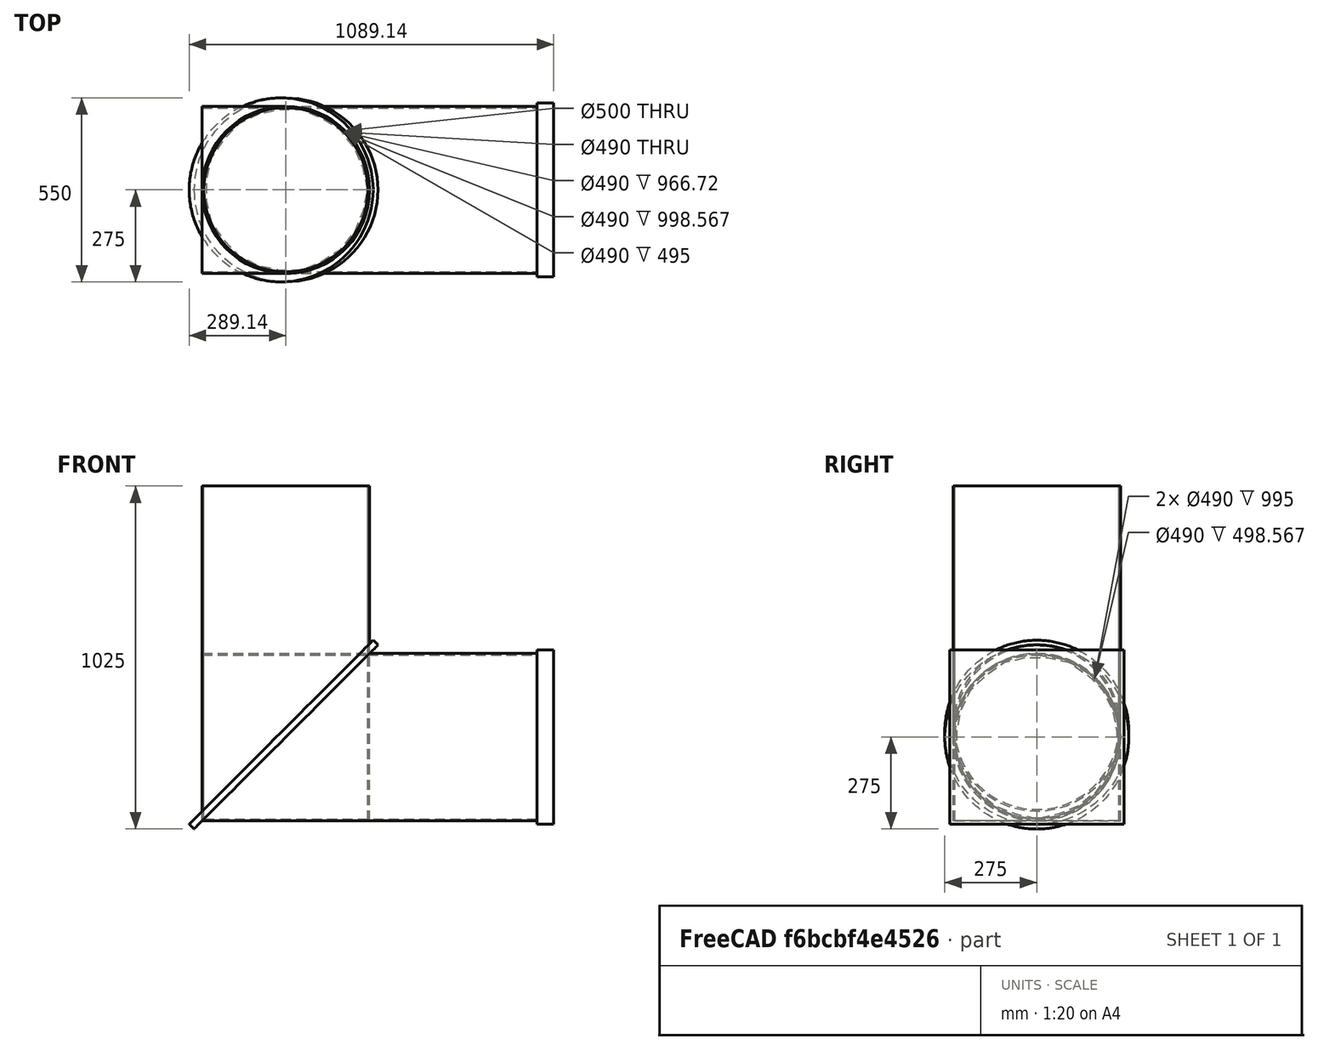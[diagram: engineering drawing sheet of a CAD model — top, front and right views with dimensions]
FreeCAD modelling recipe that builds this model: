
FCSTD DOCUMENT  (FreeCAD 0.21R33694 (Git))
Label: Tube_Corner
License: All rights reserved
LicenseURL: http://en.wikipedia.org/wiki/All_rights_reserved
objects: Part::FeaturePython×7, Part::Feature×3, Part::Plane×2, Part::Extrusion×2, Fem::ConstraintForce×2, Sketcher::SketchObject×1, Part::Face×1, App::MaterialObjectPython×1, Fem::FemSolverObjectPython×1, Fem::ConstraintFixed×1, Fem::FemMeshObjectPython×1, Fem::FemAnalysis×1
note: 16 computed .brp shape members not serialized (recipe doc carries the construction recipe); baked Part::Feature solids carry a one-line shape summary decoded from their .brp

FEATURE [Part::FeaturePython] Tube  # WARN: FeaturePython — macro-defined, semantics opaque (R4)
  AttacherType = Attacher::AttachEngine3D
  Height = 1000
  InnerRadius = 245
  OuterRadius = 250
FEATURE [Part::FeaturePython] Tube001  # WARN: FeaturePython — macro-defined, semantics opaque (R4)
  AttacherType = Attacher::AttachEngine3D
  Height = 1000
  InnerRadius = 245
  OuterRadius = 250
  Placement = pos=(-250,0,250) rot=(0,1,0;1.5708rad)
FEATURE [Part::Plane] Plane
  AttacherType = Attacher::AttachEngine3D
  Length = 1000
  Placement = pos=(-250,-250,0) rot=(0,-1,0;0.785398rad)
  Width = 500
FEATURE [Part::Plane] Plane001
  AttacherType = Attacher::AttachEngine3D
  Length = 1000
  Placement = pos=(-250,-250,0) rot=(0,-1,0;0.785398rad)
  Width = 500
FEATURE [Part::FeaturePython] Slice  # WARN: FeaturePython — macro-defined, semantics opaque (R4)
  Base = -> Tube
  Mode = 1
  Tolerance = 0
  Tools = -> [Plane]
FEATURE [Part::FeaturePython] Slice001  # WARN: FeaturePython — macro-defined, semantics opaque (R4)
  Base = -> Tube001
  Mode = 1
  Tolerance = 0
  Tools = -> [Plane001]
FEATURE [Sketcher::SketchObject] Sketch
  FullyConstrained = true
  MapMode = 5
  Placement = pos=(750,0,1.67e-13) rot=(0.57735,0.57735,0.57735;2.0944rad)
  sketch-geometry (4):
    g0: LineSegment StartX=-260 StartY=510 StartZ=0 EndX=260 EndY=510 EndZ=0
    g1: LineSegment StartX=260 StartY=510 StartZ=0 EndX=260 EndY=-10 EndZ=0
    g2: LineSegment StartX=260 StartY=-10 StartZ=0 EndX=-260 EndY=-10 EndZ=0
    g3: LineSegment StartX=-260 StartY=-10 StartZ=0 EndX=-260 EndY=510 EndZ=0
  constraints (12):
    c: Coincident(g0,g1)
    c: Coincident(g1,g2)
    c: Coincident(g2,g3)
    c: Coincident(g3,g0)
    c: Horizontal(g0)
    c: Horizontal(g2)
    c: Vertical(g1)
    c: Vertical(g3)
    c: DistanceY(g1,g-1) = 10
    c: DistanceX(g2,g-1) = 260
    c: DistanceX(g-1,g1) = 260
    c: DistanceY(g1,g1) = 520
FEATURE [Part::Face] Face
  FaceMakerClass = Part::FaceMakerBullseye
  Sources = -> [Sketch]
FEATURE [Part::Extrusion] Extrude
  Base = -> Face
  Dir = (1,0,0)
  DirMode = 2
  FaceMakerClass = Part::FaceMakerBullseye
  LengthFwd = 50
  LengthRev = 0
  Solid = false
  Symmetric = false
FEATURE [App::MaterialObjectPython] MaterialSolid  # material (typed FeaturePython)
  Category = 0
  Material = AuthorAndLicense=(c) 2014 M. Münch - GNU Lesser General Public License (LGPL),CardName=Steel-St-E-315,Density=7800 kg/m^3,Father=Metal,+13 more (map truncated)
FEATURE [Fem::FemSolverObjectPython] SolverCcxTools  # FEM object (typed FeaturePython)
  AnalysisType = 0
  BeamShellResultOutput3D = false
  BucklingFactors = 1
  EigenmodeHighLimit = 1000000
  EigenmodeLowLimit = 0
  EigenmodesCount = 10
  GeometricalNonlinearity = 0
  IterationsControlParameterCutb = 0.25,0.5,0.75,0.85,,,1.5,
  IterationsControlParameterIter = 4,8,9,200,10,400,,200,,
  IterationsControlParameterTimeUse = false
  IterationsThermoMechMaximum = 2000
  IterationsUserDefinedIncrementations = false
  IterationsUserDefinedTimeStepLength = false
  MaterialNonlinearity = 0
  MatrixSolverType = 0
  SplitInputWriter = false
  ThermoMechSteadyState = true
  TimeEnd = 1
  TimeInitialStep = 0.01
FEATURE [Part::Feature] Solid
  shape: bbox 500 x 500 x 1000 mm, 4 faces (baked)
FEATURE [Part::Feature] Solid001
  shape: bbox 1000 x 500 x 500 mm, 4 faces (baked)
FEATURE [Part::FeaturePython] BooleanFragments  # WARN: FeaturePython — macro-defined, semantics opaque (R4)
  Mode = 2
  Objects = -> [Extrude,Solid,Solid001]
  Tolerance = 0
FEATURE [Fem::ConstraintFixed] ConstraintFixed
  NormalDirection = (0,0,1)
  References = -> [BooleanFragments]
  Scale = 24
FEATURE [Fem::ConstraintForce] ConstraintForce
  Direction = -> Extrude [Edge5]
  DirectionVector = (1,2e-16,2e-16)
  Force = 1000000
  NormalDirection = (0,0,-1)
  Points = (16) [(800,260,-10),(800,86.6667,-10),(800,-86.6667,-10),(800,-260,-10),(783.333,260,-10),(783.333,86.6667,-10),(783.333,-86.6667,-10),(783.333,-260,-10),+8 more]
  References = -> [BooleanFragments]
  Scale = 18
FEATURE [Fem::ConstraintForce] ConstraintForce001
  Direction = -> Extrude [Edge2]
  DirectionVector = (-1,-2e-16,-2e-16)
  Force = 1000000
  NormalDirection = (0,0,1)
  Points = (16) [(800,-260,510),(800,-86.6667,510),(800,86.6667,510),(800,260,510),(783.333,-260,510),(783.333,-86.6667,510),(783.333,86.6667,510),(783.333,260,510),+8 more]
  References = -> [BooleanFragments]
  Reversed = true
  Scale = 18
FEATURE [Part::Feature] Face003
  shape: bbox 550.1 x 550.2 x 550.1 mm, 1 faces, 0 solids (baked)
FEATURE [Part::FeaturePython] Clone  label="Face004"  # Draft clone (typed FeaturePython)
  AttacherType = Attacher::AttachEngine3D
  Fuse = false
  Objects = -> [Face003]
  Placement = pos=(0,0,-25) rot=(0,0,1;0rad)
  Scale = (1.1,1.1,1.1)
FEATURE [Part::Extrusion] Extrude001
  Base = -> Clone
  Dir = (-1,0,1)
  DirMode = 0
  FaceMakerClass = Part::FaceMakerBullseye
  LengthFwd = 20
  LengthRev = 0
  Solid = false
  Symmetric = false
FEATURE [Part::FeaturePython] BooleanFragments001  # WARN: FeaturePython — macro-defined, semantics opaque (R4)
  Mode = 2
  Objects = -> [BooleanFragments,Extrude001]
  Tolerance = 0
FEATURE [Fem::FemMeshObjectPython] FEMMeshGmsh  # FEM object (typed FeaturePython)
  Algorithm2D = 0
  Algorithm3D = 0
  CharacteristicLengthMax = 30
  CharacteristicLengthMin = 0
  CoherenceMesh = true
  ElementDimension = 0
  ElementOrder = 1
  GeometryTolerance = 1e-06
  GroupsOfNodes = false
  HighOrderOptimize = 0
  MeshSizeFromCurvature = 12
  OptimizeNetgen = false
  OptimizeStd = true
  Part = -> BooleanFragments001
  RecombinationAlgorithm = 0
  Recombine3DAll = false
  RecombineAll = false
  SecondOrderLinear = false
FEATURE [Fem::FemAnalysis] Analysis
  Group = -> [ConstraintFixed,ConstraintForce,ConstraintForce001,MaterialSolid,SolverCcxTools,FEMMeshGmsh]
